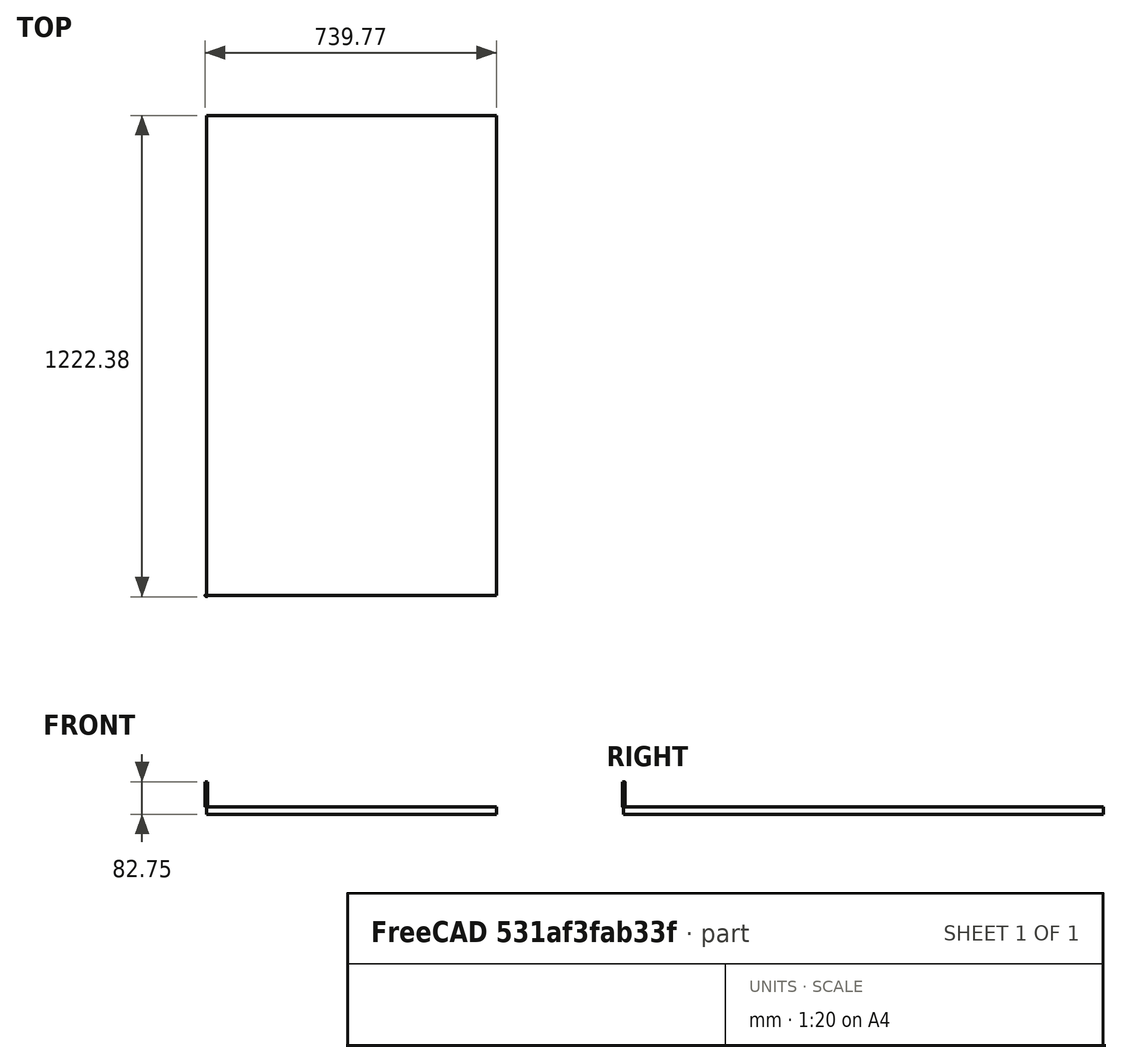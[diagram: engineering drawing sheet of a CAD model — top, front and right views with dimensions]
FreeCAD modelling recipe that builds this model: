
FCSTD DOCUMENT  (FreeCAD 0.21R33771 (Git))
Label: front_panel
License: Creative Commons Attribution-NonCommercial-ShareAlike 4.0
LicenseURL: https://creativecommons.org/licenses/by-nc-sa/4.0/
objects: Path::FeaturePython×10, Part::Box×5, Part::FeaturePython×5, App::DocumentObjectGroup×3, Part::Cylinder×2, Part::MultiFuse×1, Part::Cut×1, App::FeaturePython×1
note: 17 computed .brp shape members not serialized (recipe doc carries the construction recipe); baked Part::Feature solids carry a one-line shape summary decoded from their .brp

FEATURE [Part::Box] cube
  AttacherType = Attacher::AttachEngine3D
  Height = 9.6266
  Length = 635
  Width = 635
FEATURE [Part::Cylinder] cylinder
  Angle = 360
  AttacherType = Attacher::AttachEngine3D
  FirstAngle = 0
  Height = 9.6266
  Radius = 25.4
  SecondAngle = 0
FEATURE [Part::FeaturePython] minkowski  # WARN: FeaturePython — macro-defined, semantics opaque (R4)
  Arguments = {'convexity': '0'}
  Children = -> [cube,cylinder]
  Operation = minkowski
  Placement = pos=(25.4,25.4,0) rot=(0,0,1;0rad)
FEATURE [Part::Cylinder] cylinder001
  Angle = 360
  AttacherType = Attacher::AttachEngine3D
  FirstAngle = 0
  Height = 254
  Placement = pos=(342.9,342.9,-127) rot=(0,0,1;0rad)
  Radius = 275.272
  SecondAngle = 0
FEATURE [Part::Box] cube001
  AttacherType = Attacher::AttachEngine3D
  Height = 10.525
  Length = 736.6
  Placement = pos=(-25.4,20.6375,9.7282) rot=(0,0,1;0rad)
  Width = 8.73125
FEATURE [Part::Box] cube002
  AttacherType = Attacher::AttachEngine3D
  Height = 10.525
  Length = 736.6
  Placement = pos=(-25.4,656.431,9.7282) rot=(0,0,1;0rad)
  Width = 8.73125
FEATURE [Part::Box] cube003
  AttacherType = Attacher::AttachEngine3D
  Height = 10.525
  Length = 8.73125
  Placement = pos=(20.6375,29.2687,9.7282) rot=(0,0,1;0rad)
  Width = 627.539
FEATURE [Part::Box] cube004
  AttacherType = Attacher::AttachEngine3D
  Height = 10.525
  Length = 8.73125
  Placement = pos=(656.431,29.2687,9.7282) rot=(0,0,1;0rad)
  Width = 627.539
FEATURE [Part::MultiFuse] union
  Shapes = -> [cylinder001,cube001,cube002,cube003,cube004]
FEATURE [Part::Cut] difference
  Base = -> minkowski
  Placement = pos=(0,0,-19.2532) rot=(0,0,1;0rad)
  Tool = -> union
FEATURE [App::FeaturePython] SetupSheet  # Path/CAM operation (typed FeaturePython)
  ClearanceHeightExpression = OpStockZMax+SetupSheet.ClearanceHeightOffset
  ClearanceHeightOffset = 5
  CoolantMode = 0
  CoolantModes = None | Flood | Mist
  FinalDepthExpression = OpFinalDepth
  HorizRapid = 423.333
  SafeHeightExpression = OpStockZMax+SetupSheet.SafeHeightOffset
  SafeHeightOffset = 3
  StartDepthExpression = OpStartDepth
  StepDownExpression = OpToolDiameter
  VertRapid = 127
FEATURE [Part::FeaturePython] Clone  label="Model-difference"  # Draft clone (typed FeaturePython)
  AttacherType = Attacher::AttachEngine3D
  Fuse = false
  Objects = -> [difference]
  PathResource = Model
  Placement = pos=(25.4,25.7079,-19.2532) rot=(0,0,1;0rad)
  Scale = (1,1,1)
FEATURE [App::DocumentObjectGroup] Model
  Group = -> [Clone]
FEATURE [Part::FeaturePython] Stock  # WARN: FeaturePython — macro-defined, semantics opaque (R4)
  Height = 19.2532
  Length = 736.6
  Placement = pos=(3.8147e-07,0.00790062,-19.2532) rot=(0,0,1;0rad)
  StockType = CreateBox
  Width = 1219.2
FEATURE [Part::FeaturePython] ToolBit  label="SpeTool 1/4" Downcut Carbide End Mill002"  # Path/CAM toolbit (typed FeaturePython)
  BitPropertyNames = Chipload | CuttingEdgeHeight | Diameter | Flutes | Length | Material | ShankDiameter | SpindleDirection
  BitShape = <path>
  Chipload = 0
  CuttingEdgeHeight = 25.4
  Diameter = 6.35
  Flutes = 2
  Length = 63.5
  Material = 1
  ShankDiameter = 6.35
  ShapeName = endmill
  SpindleDirection = 0
FEATURE [Path::FeaturePython] SpeTool_1_4__Downcut_Carbide_End_Mill  label="SpeTool 1/4" Downcut Carbide End Mill001"  # Path/CAM operation (typed FeaturePython)
  HorizFeed = 42.3333
  HorizRapid = 423.333
  SpindleDir = 0
  SpindleSpeed = 12000
  Tool = -> ToolBit
  ToolNumber = 2
  VertFeed = 12.7
  VertRapid = 127
  expr: HorizRapid = SetupSheet.HorizRapid
  expr: VertRapid = SetupSheet.VertRapid
FEATURE [Part::FeaturePython] ToolBit002  label="SpeTool 3/16" Downcut Carbide End Mill"  # Path/CAM toolbit (typed FeaturePython)
  BitPropertyNames = Chipload | CuttingEdgeHeight | Diameter | Flutes | Length | Material | ShankDiameter | SpindleDirection
  BitShape = <path>
  Chipload = 0
  CuttingEdgeHeight = 25.4
  Diameter = 4.7498
  File = <userpath>/.config/FreeCAD-tools/Bit/3-16inch_endmill.fctb
  Flutes = 2
  Length = 63.5
  Material = 1
  ShankDiameter = 6.35
  ShapeName = endmill
  SpindleDirection = 0
FEATURE [Path::FeaturePython] SpeTool_3_16__Downcut_Carbide_End_Mill  label="SpeTool 3/16" Downcut Carbide End Mill001"  # Path/CAM operation (typed FeaturePython)
  HorizFeed = 42.3333
  HorizRapid = 423.333
  SpindleDir = 0
  SpindleSpeed = 12000
  Tool = -> ToolBit002
  ToolNumber = 3
  VertFeed = 8.46667
  VertRapid = 127
  expr: HorizRapid = SetupSheet.HorizRapid
  expr: VertRapid = SetupSheet.VertRapid
FEATURE [App::DocumentObjectGroup] Tools
  Group = -> [SpeTool_1_4__Downcut_Carbide_End_Mill,SpeTool_3_16__Downcut_Carbide_End_Mill]
FEATURE [Path::FeaturePython] Profile  label="ProfileCircle"  # Path/CAM operation (typed FeaturePython)
  Active = true
  AreaParams:
    Tolerance = 1e-07
    FitArcs = True
    Simplify = False
    CleanDistance = 0.0
    Accuracy = 0.01
    Unit = 1.0
    MinArcPoints = 4
    MaxArcPoints = 100
    ClipperScale = 10000000.0
    Fill = 0
    Coplanar = 0
    Reorient = True
    Outline = False
    Explode = False
    OpenMode = 0
    Deflection = 0.01
    SubjectFill = 0
    ClipFill = 0
    Offset = -3.175
    ExtraPass = 0
    Stepover = 0.0
    LastStepover = 0.0
    JoinType = 0
    EndType = 0
    MiterLimit = 2.0
    RoundPrecision = 0.0
    PocketMode = 0
    ToolRadius = 1.0
    PocketExtraOffset = 0.0
    PocketStepover = 0.0
    PocketLastStepover = 0.0
    FromCenter = False
    Angle = 45.0
    AngleShift = 0.0
    Shift = 0.0
    Thicken = False
    SectionCount = -1
    Stepdown = 1.0
    SectionOffset = 0.0
    SectionTolerance = 1e-07
    SectionMode = 2
    Project = False
  Base = -> [Clone]
  ClearanceHeight = 5
  CoolantMode = 0
  CycleTime = 00:02:03
  Direction = 0
  FinalDepth = -19.2532
  HandleMultipleFeatures = 0
  JoinType = 0
  MiterLimit = 0.1
  OffsetExtra = 0
  OpFinalDepth = -19.2532
  OpStartDepth = 0
  OpStockZMax = 0
  OpStockZMin = -19.2532
  OpToolDiameter = 6.35
  PathParams = {'orientation': 1, 'feedrate': 42.333333333333336, 'feedrate_v': 12.7, 'verbose': True, 'resume_height': 3.0, 'retraction': 5.0, 'return_end': True, 'preamble': False}
  SafeHeight = 3
  Side = 1
  SplitArcs = false
  StartDepth = 0
  StartPoint = (0,0,0)
  StepDown = 6.35
  ToolController = -> SpeTool_1_4__Downcut_Carbide_End_Mill
  UseComp = true
  UseStartPoint = false
  processCircles = false
  processHoles = false
  processPerimeter = true
  expr: ClearanceHeight = OpStockZMax + SetupSheet.ClearanceHeightOffset
  expr: FinalDepth = OpFinalDepth
  expr: SafeHeight = OpStockZMax + SetupSheet.SafeHeightOffset
  expr: StartDepth = OpStartDepth
  expr: StepDown = OpToolDiameter
FEATURE [Path::FeaturePython] Profile001  label="ProfilePerimeter"  # Path/CAM operation (typed FeaturePython)
  Active = true
  AreaParams:
    Tolerance = 1e-07
    FitArcs = True
    Simplify = False
    CleanDistance = 0.0
    Accuracy = 0.01
    Unit = 1.0
    MinArcPoints = 4
    MaxArcPoints = 100
    ClipperScale = 10000000.0
    Fill = 0
    Coplanar = 0
    Reorient = True
    Outline = False
    Explode = False
    OpenMode = 0
    Deflection = 0.01
    SubjectFill = 0
    ClipFill = 0
    Offset = 3.175
    ExtraPass = 0
    Stepover = 0.0
    LastStepover = 0.0
    JoinType = 0
    EndType = 0
    MiterLimit = 2.0
    RoundPrecision = 0.0
    PocketMode = 0
    ToolRadius = 1.0
    PocketExtraOffset = 0.0
    PocketStepover = 0.0
    PocketLastStepover = 0.0
    FromCenter = False
    Angle = 45.0
    AngleShift = 0.0
    Shift = 0.0
    Thicken = False
    SectionCount = -1
    Stepdown = 1.0
    SectionOffset = 0.0
    SectionTolerance = 1e-07
    SectionMode = 2
    Project = False
  Base = -> [Clone]
  ClearanceHeight = 5
  CoolantMode = 0
  CycleTime = 00:04:17
  Direction = 0
  FinalDepth = -19.2532
  HandleMultipleFeatures = 0
  JoinType = 0
  MiterLimit = 0.1
  OffsetExtra = 0
  OpFinalDepth = -19.2532
  OpStartDepth = 0
  OpStockZMax = 0
  OpStockZMin = -19.2532
  OpToolDiameter = 6.35
  PathParams = {'orientation': 1, 'feedrate': 42.333333333333336, 'feedrate_v': 12.7, 'verbose': True, 'resume_height': 3.0, 'retraction': 5.0, 'return_end': True, 'preamble': False}
  SafeHeight = 3
  Side = 0
  SplitArcs = false
  StartDepth = 0
  StartPoint = (0,0,0)
  StepDown = 6.35
  ToolController = -> SpeTool_1_4__Downcut_Carbide_End_Mill
  UseComp = true
  UseStartPoint = false
  processCircles = false
  processHoles = false
  processPerimeter = true
  expr: ClearanceHeight = OpStockZMax + SetupSheet.ClearanceHeightOffset
  expr: FinalDepth = OpFinalDepth
  expr: SafeHeight = OpStockZMax + SetupSheet.SafeHeightOffset
  expr: StartDepth = OpStartDepth
  expr: StepDown = OpToolDiameter
FEATURE [Path::FeaturePython] DressupTag  # Path/CAM operation (typed FeaturePython)
  Angle = 45
  Base = -> Profile001
  Height = 6.35
  Positions = (8) [(209.108,714.672,0),(527.325,714.674,0),(714.374,527.424,0),(714.375,209.88,0),(527.491,22.5441,0),(209.275,22.5419,0),(22.2259,209.792,0),(22.2253,527.336,0)]
  Radius = 0
  SegmentationFactor = 50
  Width = 63.5
FEATURE [Path::FeaturePython] RampEntryDressup  label="RampEntryPerimeter"  # Path/CAM operation (typed FeaturePython)
  Angle = 60
  Base = -> DressupTag
  CustomFeedRate = 0
  DressupStartDepth = 0
  Method = 2
  RampFeedRate = 0
  UseStartDepth = false
FEATURE [Path::FeaturePython] DressupTag001  # Path/CAM operation (typed FeaturePython)
  Angle = 45
  Base = -> Profile
  Height = 6.35
  Positions = (6) [(619.24,473.801,0),(620.99,267.691,0),(477.739,119.49,0),(180.857,171.373,0),(114.35,466.313,0),(257.824,617.268,0)]
  Radius = 0
  SegmentationFactor = 50
  Width = 63.5
FEATURE [Path::FeaturePython] RampEntryDressup001  label="RampEntryCircle"  # Path/CAM operation (typed FeaturePython)
  Angle = 60
  Base = -> DressupTag001
  CustomFeedRate = 0
  DressupStartDepth = 0
  Method = 2
  RampFeedRate = 0
  UseStartDepth = false
FEATURE [Path::FeaturePython] Pocket_Shape  # Path/CAM operation (typed FeaturePython)
  Active = true
  AreaParams:
    Tolerance = 1e-07
    FitArcs = True
    Simplify = False
    CleanDistance = 0.0
    Accuracy = 0.01
    Unit = 1.0
    MinArcPoints = 4
    MaxArcPoints = 100
    ClipperScale = 10000000.0
    Fill = 0
    Coplanar = 0
    Reorient = True
    Outline = False
    Explode = False
    OpenMode = 0
    Deflection = 0.01
    SubjectFill = 0
    ClipFill = 0
    Offset = 0.0
    ExtraPass = 0
    Stepover = 0.0
    LastStepover = 0.0
    JoinType = 0
    EndType = 0
    MiterLimit = 2.0
    RoundPrecision = 0.0
    PocketMode = 2
    ToolRadius = 2.3749
    PocketExtraOffset = 0.0
    PocketStepover = 2.3749
    PocketLastStepover = 0.0
    FromCenter = True
    Angle = 45.0
    AngleShift = 0.0
    Shift = 0.0
    Thicken = False
    SectionCount = -1
    Stepdown = 1.0
    SectionOffset = 0.0
    SectionTolerance = 1e-07
    SectionMode = 2
    Project = False
  Base = -> [Clone]
  ClearanceHeight = 5
  CoolantMode = 0
  CutMode = 0
  CycleTime = 00:13:05
  ExtensionCorners = true
  ExtensionFeature = -> [Clone]
  ExtensionLengthDefault = 4.7498
  ExtraOffset = 0
  FinalDepth = -9.525
  FinishDepth = 2.54
  KeepToolDown = false
  MinTravel = false
  OffsetPattern = 1
  OpFinalDepth = -9.525
  OpStartDepth = 2.65503e-07
  OpStockZMax = 0
  OpStockZMin = -19.2532
  OpToolDiameter = 4.7498
  PathParams = {'orientation': 1, 'feedrate': 42.333333333333336, 'feedrate_v': 8.466666666666667, 'verbose': True, 'resume_height': 3.0, 'retraction': 5.0, 'return_end': True, 'preamble': False}
  PocketLastStepOver = 0
  SafeHeight = 3
  SplitArcs = false
  StartAt = 0
  StartDepth = 2.65503e-07
  StartPoint = (0,0,0)
  StepDown = 4.7498
  StepOver = 50
  ToolController = -> SpeTool_3_16__Downcut_Carbide_End_Mill
  UseOutline = false
  UseStartPoint = false
  ZigZagAngle = 45
  expr: ClearanceHeight = OpStockZMax + SetupSheet.ClearanceHeightOffset
  expr: ExtensionLengthDefault = OpToolDiameter
  expr: FinalDepth = OpFinalDepth
  expr: SafeHeight = OpStockZMax + SetupSheet.SafeHeightOffset
  expr: StartDepth = OpStartDepth
  expr: StepDown = OpToolDiameter
FEATURE [App::DocumentObjectGroup] Operations
  Group = -> [RampEntryDressup001,Pocket_Shape,RampEntryDressup]
FEATURE [Path::FeaturePython] Job  label="FrontPanel"  # Path/CAM operation (typed FeaturePython)
  CycleTime = 00:19:25
  Fixtures = G54
  GeometryTolerance = 0
  JobType = 0
  LastPostProcessDate = 2024-07-14 10:37:07.945218
  LastPostProcessOutput = <userpath>/GIT/cnc-projects/shophacks_ultimate_air_filter/front_panel.gcode
  Model = -> Model
  Operations = -> Operations
  OrderOutputBy = 0
  PostProcessor = 14
  PostProcessorArgs = --inches
  PostProcessorOutputFile = <userpath>/GIT/cnc-projects/shophacks_ultimate_air_filter/front_panel.gcode
  SetupSheet = -> SetupSheet
  SplitOutput = false
  Stock = -> Stock
  Tools = -> Tools
note: 2 file-system paths scrubbed to <path> (originals preserved in the JSON sidecar)
